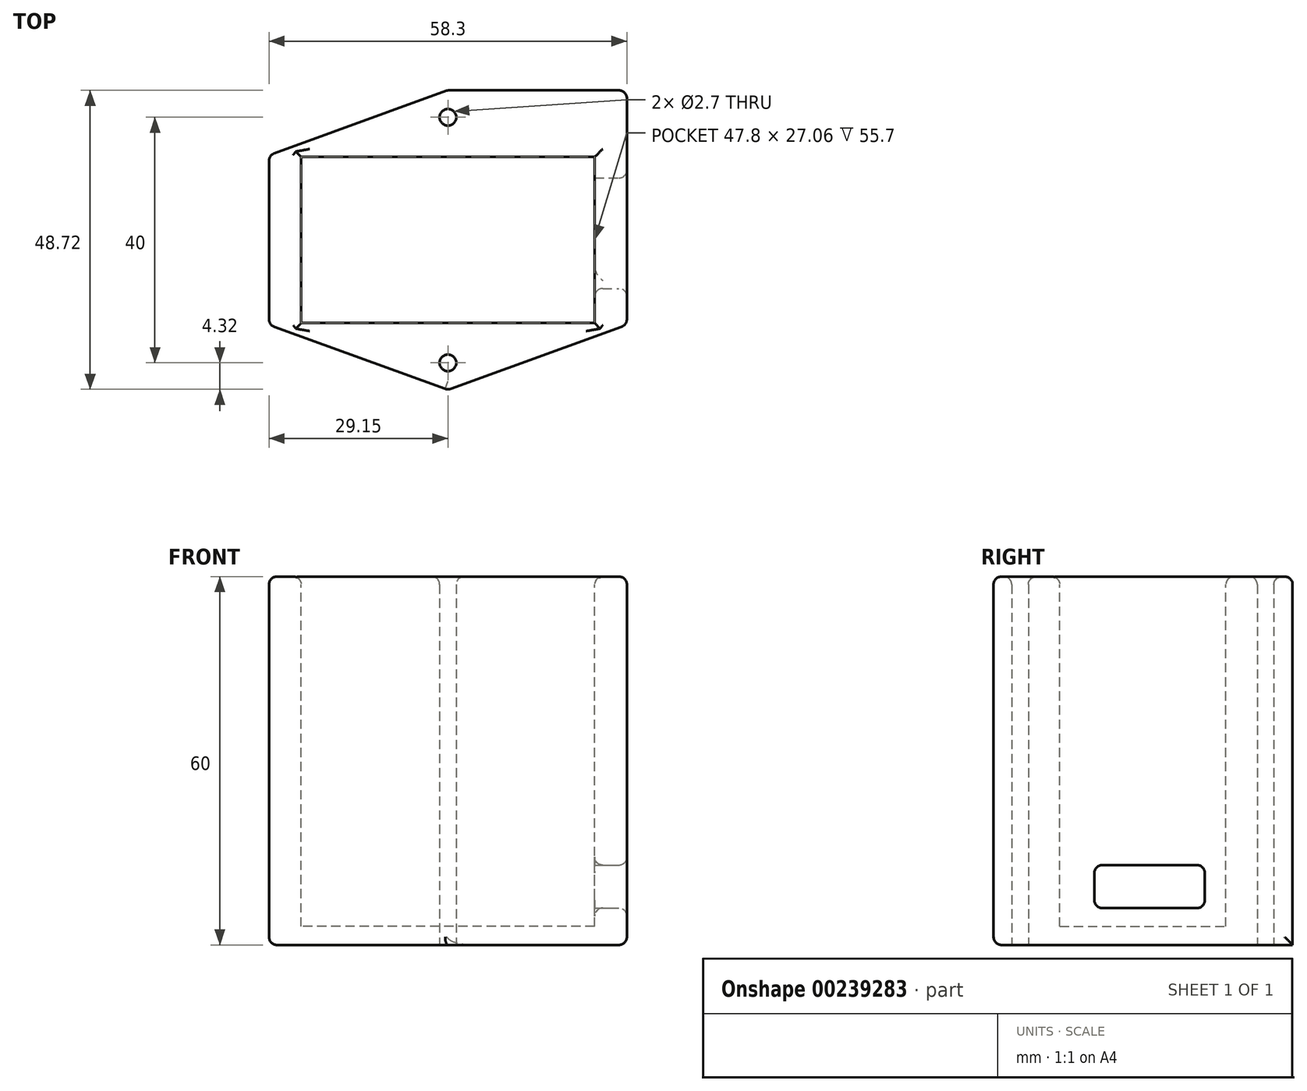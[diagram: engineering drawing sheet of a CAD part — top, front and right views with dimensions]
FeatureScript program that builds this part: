
annotation { "Feature Type Name" : "Feature", "Feature Type Description" : "" }
export const myFeature = defineFeature(function(context is Context, id is Id, definition is map)
    precondition{}
    {
        {
            var Q0;
            Q0=qCreatedBy(makeId("Top.planeOp"),FACE);
            var sketch = newSketch(context, id + "F0", { "sketchPlane" : qUnion([Q0])});
            skLineSegment(sketch, "E0", {"start": v(-29.15, 13.8) * mm, "end": v(0, 24.4) * mm});
            skLineSegment(sketch, "E1", {"start": v(0, 24.4) * mm, "end": v(29.15, 24.4) * mm});
            skLineSegment(sketch, "E2", {"start": v(29.15, 24.4) * mm, "end": v(29.15, -13.8) * mm});
            skLineSegment(sketch, "E3", {"start": v(29.15, -13.8) * mm, "end": v(0, -24.4) * mm});
            skLineSegment(sketch, "E4", {"start": v(0, -24.4) * mm, "end": v(-29.15, -13.8) * mm});
            skLineSegment(sketch, "E5", {"start": v(-29.15, -13.8) * mm, "end": v(-29.15, 13.8) * mm});
            skCircle(sketch, "E6", {"center": v(0, 20) * mm, "radius": 1.35 * mm});
            skCircle(sketch, "E7", {"center": v(0, -20) * mm, "radius": 1.35 * mm});
            skSolve(sketch);
        }
        {
            var Q0;
            Q0=makeQuery(id+"F0.imprint","IMPRINT",FACE,{"disambiguationData":[TD([[makeQuery(id+"F0.imprint","IMPRINT",EDGE,{"derivedFrom":sQuery(id+"F0.wireOp",EDGE,"E0")}),-1.0]])]});
            extrude(context, id + "F1", {"entities" : qUnion([Q0]), "depth" : 60 * mm});
        }
        {
            var Q0;
            Q0=makeQuery(id+"F1.opExtrude","CAP_FACE",FACE,{"disambiguationData":[OSD([sQuery(id+"F0.wireOp",EDGE,"E0"),sQuery(id+"F0.wireOp",EDGE,"E1"),sQuery(id+"F0.wireOp",EDGE,"E2"),sQuery(id+"F0.wireOp",EDGE,"E3"),sQuery(id+"F0.wireOp",EDGE,"E4"),sQuery(id+"F0.wireOp",EDGE,"E5"),sQuery(id+"F0.wireOp",EDGE,"E6"),sQuery(id+"F0.wireOp",EDGE,"E7")])],"isStart":false});
            var sketch = newSketch(context, id + "F2", { "sketchPlane" : qUnion([Q0])});
            skLineSegment(sketch, "E8.bottom", {"start": v(23.9, -13.53) * mm, "end": v(-23.9, -13.53) * mm});
            skLineSegment(sketch, "E8.top", {"start": v(23.9, 13.53) * mm, "end": v(-23.9, 13.53) * mm});
            skLineSegment(sketch, "E8.left", {"start": v(23.9, -13.53) * mm, "end": v(23.9, 13.53) * mm});
            skLineSegment(sketch, "E8.right", {"start": v(-23.9, -13.53) * mm, "end": v(-23.9, 13.53) * mm});
            skPoint(sketch, "E8.middle", {"position": v(0, 0) * mm});
            skSolve(sketch);
        }
        {
            var Q0;
            Q0=makeQuery(id+"F2.imprint","IMPRINT",FACE,{"disambiguationData":[TD([[makeQuery(id+"F2.imprint","IMPRINT",EDGE,{"derivedFrom":sQuery(id+"F2.wireOp",EDGE,"E8.bottom")}),-1.0]])]});
            extrude(context, id + "F3", {"entities" : qUnion([Q0]), "operationType" : NewBodyOperationType.REMOVE, "oppositeDirection" : true, "depth" : 57 * mm});
        }
        {
            var Q0;
            Q0=makeQuery(id+"F1.opExtrude","SWEPT_FACE",FACE,{"disambiguationData":[OSD([sQuery(id+"F0.wireOp",EDGE,"E5")])]});
            var Q1;
            Q1=makeQuery(id+"F1.opExtrude","SWEPT_FACE",FACE,{"disambiguationData":[OSD([sQuery(id+"F0.wireOp",EDGE,"E4")])]});
            var Q2;
            Q2=makeQuery(id+"F1.opExtrude","SWEPT_FACE",FACE,{"disambiguationData":[OSD([sQuery(id+"F0.wireOp",EDGE,"E3")])]});
            var Q3;
            Q3=makeQuery(id+"F1.opExtrude","SWEPT_FACE",FACE,{"disambiguationData":[OSD([sQuery(id+"F0.wireOp",EDGE,"E0")])]});
            var Q4;
            Q4=makeQuery(id+"F3.boolean.opBoolean","COPY",EDGE,{"derivedFrom":makeQuery(id+"F3.opExtrude","CAP_EDGE",EDGE,{"disambiguationData":[OSD([sQuery(id+"F2.wireOp",EDGE,"E8.bottom")])],"isStart":true})});
            var Q5;
            Q5=makeQuery(id+"F3.boolean.opBoolean","COPY",EDGE,{"derivedFrom":makeQuery(id+"F3.opExtrude","CAP_EDGE",EDGE,{"disambiguationData":[OSD([sQuery(id+"F2.wireOp",EDGE,"E8.right")])],"isStart":true})});
            var Q6;
            Q6=makeQuery(id+"F3.boolean.opBoolean","COPY",EDGE,{"derivedFrom":makeQuery(id+"F3.opExtrude","CAP_EDGE",EDGE,{"disambiguationData":[OSD([sQuery(id+"F2.wireOp",EDGE,"E8.top")])],"isStart":true})});
            var Q7;
            Q7=makeQuery(id+"F1.opExtrude","CAP_FACE",FACE,{"disambiguationData":[OSD([sQuery(id+"F0.wireOp",EDGE,"E0"),sQuery(id+"F0.wireOp",EDGE,"E1"),sQuery(id+"F0.wireOp",EDGE,"E2"),sQuery(id+"F0.wireOp",EDGE,"E3"),sQuery(id+"F0.wireOp",EDGE,"E4"),sQuery(id+"F0.wireOp",EDGE,"E5"),sQuery(id+"F0.wireOp",EDGE,"E6"),sQuery(id+"F0.wireOp",EDGE,"E7")])],"isStart":false});
            fillet(context, id + "F4", {"entities" : qUnion([Q0, Q1, Q2, Q3, Q4, Q5, Q6, Q7]), "radius" : 1.3 * mm, "tangentPropagation" : true, "allowEdgeOverflow" : false});
        }
        {
            var Q0;
            Q0=makeQuery(id+"F1.opExtrude","SWEPT_FACE",FACE,{"disambiguationData":[OSD([sQuery(id+"F0.wireOp",EDGE,"E2")])]});
            cPlane(context, id + "F5", {"entities" : qUnion([Q0]), "cplaneType" : CPlaneType.OFFSET, "offset" : 0 * mm, "width" : 150 * mm, "height" : 150 * mm});
        }
        {
            var Q0;
            Q0=qCreatedBy(id+"F5.planeOp",FACE);
            var sketch = newSketch(context, id + "F6", { "sketchPlane" : qUnion([Q0])});
            skLineSegment(sketch, "E9.bottom", {"start": v(10.11, 6) * mm, "end": v(-7.89, 6) * mm});
            skLineSegment(sketch, "E9.top", {"start": v(10.11, 13) * mm, "end": v(-7.89, 13) * mm});
            skLineSegment(sketch, "E9.left", {"start": v(10.11, 6) * mm, "end": v(10.11, 13) * mm});
            skLineSegment(sketch, "E9.right", {"start": v(-7.89, 6) * mm, "end": v(-7.89, 13) * mm});
            skSolve(sketch);
        }
        {
            var Q0;
            Q0=makeQuery(id+"F6.imprint","IMPRINT",FACE,{"disambiguationData":[TD([[makeQuery(id+"F6.imprint","IMPRINT",EDGE,{"derivedFrom":sQuery(id+"F6.wireOp",EDGE,"E9.bottom")}),-1.0]])]});
            extrude(context, id + "F7", {"entities" : qUnion([Q0]), "operationType" : NewBodyOperationType.REMOVE, "oppositeDirection" : true, "depth" : 25 * mm});
        }
        {
            var Q0;
            Q0=makeQuery(id+"F7.boolean.opBoolean","COPY",EDGE,{"derivedFrom":makeQuery(id+"F7.opExtrude","CAP_EDGE",EDGE,{"disambiguationData":[OSD([sQuery(id+"F6.wireOp",EDGE,"E9.bottom")])],"isStart":true})});
            var Q1;
            Q1=makeQuery(id+"F7.boolean.opBoolean","COPY",EDGE,{"derivedFrom":makeQuery(id+"F7.opExtrude","CAP_EDGE",EDGE,{"disambiguationData":[OSD([sQuery(id+"F6.wireOp",EDGE,"E9.right")])],"isStart":true})});
            var Q2;
            Q2=makeQuery(id+"F1.opExtrude","SWEPT_FACE",FACE,{"disambiguationData":[OSD([sQuery(id+"F0.wireOp",EDGE,"E2")])]});
            var Q3;
            Q3=makeQuery(id+"F7.boolean.opBoolean","COPY",EDGE,{"derivedFrom":makeQuery(id+"F7.opExtrude","CAP_EDGE",EDGE,{"disambiguationData":[OSD([sQuery(id+"F6.wireOp",EDGE,"E9.left")])],"isStart":true})});
            var Q4;
            Q4=makeQuery(id+"F7.boolean.opBoolean","COPY",EDGE,{"derivedFrom":makeQuery(id+"F7.opExtrude","SWEPT_EDGE",EDGE,{"disambiguationData":[OSD([sQuery(id+"F6.wireOp",EDGE,"E9.top"),sQuery(id+"F6.wireOp",EDGE,"E9.left")])]})});
            var Q5;
            Q5=makeQuery(id+"F7.boolean.opBoolean","COPY",EDGE,{"derivedFrom":makeQuery(id+"F7.opExtrude","SWEPT_EDGE",EDGE,{"disambiguationData":[OSD([sQuery(id+"F6.wireOp",EDGE,"E9.bottom"),sQuery(id+"F6.wireOp",EDGE,"E9.left")])]})});
            var Q6;
            Q6=makeQuery(id+"F7.boolean.opBoolean","COPY",FACE,{"derivedFrom":makeQuery(id+"F7.opExtrude","SWEPT_FACE",FACE,{"disambiguationData":[OSD([sQuery(id+"F6.wireOp",EDGE,"E9.right")])]})});
            fillet(context, id + "F8", {"entities" : qUnion([Q0, Q1, Q2, Q3, Q4, Q5, Q6]), "radius" : 1.3 * mm, "tangentPropagation" : true, "allowEdgeOverflow" : false});
        }
    });
